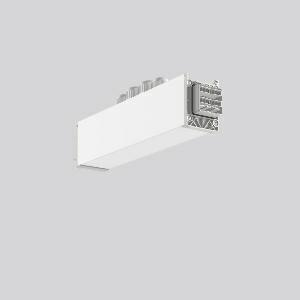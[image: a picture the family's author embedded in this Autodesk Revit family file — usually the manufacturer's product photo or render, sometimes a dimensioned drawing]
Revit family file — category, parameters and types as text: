
# Revit family: linedo_mitteleinspeisung_14pol_s_s_982698_002_2_2fc6
name_source: partatom
category: Lighting Fixtures
units: mm (PartAtom-declared; Revit-internal decimal feet)

## family parameters
Cut with Voids When Loaded = No
Host = Face
Light Source = No
Part Type = Normal
Room Calculation Point = No
Round Connector Dimension = Use Diameter
Shared = No

## types (1)
- LINEDO_Mitteleinspeisung_14pol_S_S
    Apparent Load = 0 VA
    Default Elevation = 1800 mm
    Description = Series: LINEDO
Middle power feed, 14-pole, connection plug / plug. Housing: extruded aluminium profile, powder-coated. Cover made of plastic, surface like housing. LINEDO plug system, plastic, light grey. 4 cable glands (2 x M20 and 2 x M25). Cable glands on top. Easy connection for rigid or flexible wires.
Colour: white
Length: 349 mm
Width: 58 mm
Height: 76 mm
Weight: 850 g
    Height = 76 mm
    Lamp = 0 x
    Length = 349 mm
    Luminous efficacy = 0 lm/W
    Manufacturer = RZB
    ModVariant = No
    Model = 982698.002.2
    Mounting Place = Ceiling
    Mounting Type = Surface mounted, Pendant
    Number of Poles = 1
    OnlyDefault = Yes
    Power Factor = 1
    Product Name = LINEDO_Mitteleinspeisung_14pol_S_S
    Product group = Surface mounted continuous line luminaire system
    ProductGroupID = 310
    Protection Class = Protection class I
    Protection Degree = IP 54
    RLX_Detail_Level = 1
    RLX_Emergency_Light_Flux = 0 lm
    RLX_Emergency_Type = 0
    RLX_Emergency_Type_DB = No
    RlxData = <blob elided: 20717 chars, md5=3ba9a042>
    Standby Power = 0 W
    System Light Flux = 0 lm
    System Power = 0 W
    Type Comments = Product without accessories
    Type Image = 982698.002.2.jpg
    URL = http://relux.com
    VarID = ---
    Voltage = 0 V
    Weight = 0.00 kg
    Width = 58 mm

## geometry (parser evidence)
native form markers: Blend x4, Sweep x10
no freeform markers — native parametric forms only
